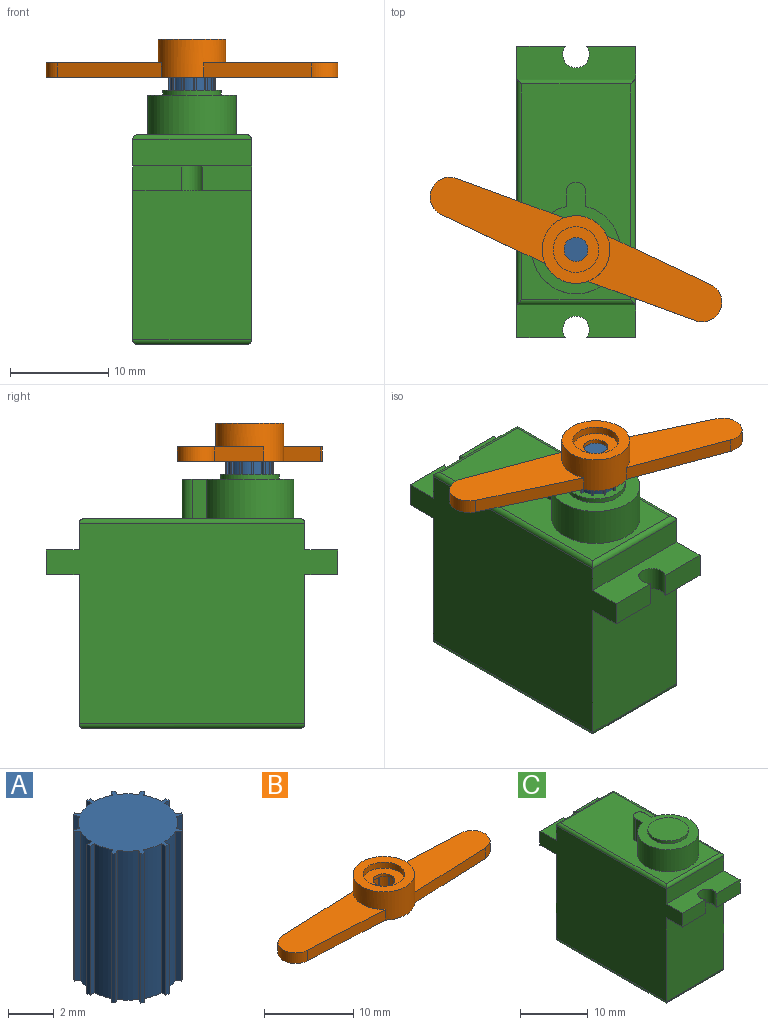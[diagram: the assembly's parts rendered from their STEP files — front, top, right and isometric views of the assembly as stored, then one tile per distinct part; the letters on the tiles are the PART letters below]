
ASSEMBLY  parts=3 mates=2
PART A: 50 faces, bbox 4.9x4.9x8 mm
  f0: cylinder r=2.45mm len=8mm, axis (0,0,-1), area 1.6mm2, adj f1,f2,f3,f4
  f1: plane 8x0.28mm, normal (-1,0,0), area 2.2mm2, adj f0,f3,f4,f5
  f2: plane 8x0.28mm, normal (1,0,0), area 2.2mm2, adj f0,f3,f4,f49
  f3: plane 4.9x4.9mm, normal (0,0,1), area 15.5mm2, adj f0,f1,f2,f5,f6,f7,f8,f9
  f4: plane 4.9x4.9mm, normal (0,0,-1), area 15.5mm2, adj f0,f1,f2,f5,f6,f7,f8,f9
  f5: cylinder r=2.17mm len=8mm, axis (0,0,-1), area 7.5mm2, adj f1,f3,f4,f8
  f6: cylinder r=2.45mm len=8mm, axis (0,0,-1), area 1.6mm2, adj f3,f4,f7,f8
  f7: plane 8x0.24mm, normal (-0.87,-0.5,0), area 2.2mm2, adj f3,f4,f6,f9
  f8: plane 8x0.24mm, normal (0.87,0.5,0), area 2.2mm2, adj f3,f4,f5,f6
  f9: cylinder r=2.17mm len=8mm, axis (0,0,-1), area 7.5mm2, adj f3,f4,f7,f12
  f10: cylinder r=2.45mm len=8mm, axis (0,0,-1), area 1.6mm2, adj f3,f4,f11,f12
  f11: plane 8x0.24mm, normal (-0.5,-0.87,0), area 2.2mm2, adj f3,f4,f10,f13
  f12: plane 8x0.24mm, normal (0.5,0.87,0), area 2.2mm2, adj f3,f4,f9,f10
  f13: cylinder r=2.17mm len=8mm, axis (0,0,-1), area 7.5mm2, adj f3,f4,f11,f16
  f14: cylinder r=2.45mm len=8mm, axis (0,0,-1), area 1.6mm2, adj f3,f4,f15,f16
  f15: plane 8x0.28mm, normal (0,-1,0), area 2.2mm2, adj f3,f4,f14,f17
  f16: plane 8x0.28mm, normal (0,1,0), area 2.2mm2, adj f3,f4,f13,f14
  f17: cylinder r=2.17mm len=8mm, axis (0,0,-1), area 7.5mm2, adj f3,f4,f15,f20
  f18: cylinder r=2.45mm len=8mm, axis (0,0,-1), area 1.6mm2, adj f3,f4,f19,f20
  f19: plane 8x0.24mm, normal (0.5,-0.87,0), area 2.2mm2, adj f3,f4,f18,f21
  f20: plane 8x0.24mm, normal (-0.5,0.87,0), area 2.2mm2, adj f3,f4,f17,f18
  f21: cylinder r=2.17mm len=8mm, axis (0,0,-1), area 7.5mm2, adj f3,f4,f19,f24
  f22: cylinder r=2.45mm len=8mm, axis (0,0,-1), area 1.6mm2, adj f3,f4,f23,f24
  f23: plane 8x0.24mm, normal (0.87,-0.5,0), area 2.2mm2, adj f3,f4,f22,f25
  f24: plane 8x0.24mm, normal (-0.87,0.5,0), area 2.2mm2, adj f3,f4,f21,f22
  f25: cylinder r=2.17mm len=8mm, axis (0,0,-1), area 7.5mm2, adj f3,f4,f23,f28
  f26: cylinder r=2.45mm len=8mm, axis (0,0,-1), area 1.6mm2, adj f3,f4,f27,f28
  f27: plane 8x0.28mm, normal (1,0,0), area 2.2mm2, adj f3,f4,f26,f29
  f28: plane 8x0.28mm, normal (-1,0,0), area 2.2mm2, adj f3,f4,f25,f26
  f29: cylinder r=2.17mm len=8mm, axis (0,0,-1), area 7.5mm2, adj f3,f4,f27,f32
  f30: cylinder r=2.45mm len=8mm, axis (0,0,-1), area 1.6mm2, adj f3,f4,f31,f32
  f31: plane 8x0.24mm, normal (0.87,0.5,0), area 2.2mm2, adj f3,f4,f30,f33
  f32: plane 8x0.24mm, normal (-0.87,-0.5,0), area 2.2mm2, adj f3,f4,f29,f30
  f33: cylinder r=2.17mm len=8mm, axis (0,0,-1), area 7.5mm2, adj f3,f4,f31,f36
  f34: cylinder r=2.45mm len=8mm, axis (0,0,-1), area 1.6mm2, adj f3,f4,f35,f36
  f35: plane 8x0.24mm, normal (0.5,0.87,0), area 2.2mm2, adj f3,f4,f34,f37
  f36: plane 8x0.24mm, normal (-0.5,-0.87,0), area 2.2mm2, adj f3,f4,f33,f34
  f37: cylinder r=2.17mm len=8mm, axis (0,0,-1), area 7.5mm2, adj f3,f4,f35,f40
  f38: cylinder r=2.45mm len=8mm, axis (0,0,-1), area 1.6mm2, adj f3,f4,f39,f40
  f39: plane 8x0.28mm, normal (0,1,0), area 2.2mm2, adj f3,f4,f38,f41
  f40: plane 8x0.28mm, normal (0,-1,0), area 2.2mm2, adj f3,f4,f37,f38
  f41: cylinder r=2.17mm len=8mm, axis (0,0,-1), area 7.5mm2, adj f3,f4,f39,f44
  f42: cylinder r=2.45mm len=8mm, axis (0,0,-1), area 1.6mm2, adj f3,f4,f43,f44
  f43: plane 8x0.24mm, normal (-0.5,0.87,0), area 2.2mm2, adj f3,f4,f42,f45
  f44: plane 8x0.24mm, normal (0.5,-0.87,0), area 2.2mm2, adj f3,f4,f41,f42
  f45: cylinder r=2.17mm len=8mm, axis (0,0,-1), area 7.5mm2, adj f3,f4,f43,f48
  f46: cylinder r=2.45mm len=8mm, axis (0,0,-1), area 1.6mm2, adj f3,f4,f47,f48
  f47: plane 8x0.24mm, normal (-0.87,0.5,0), area 2.2mm2, adj f3,f4,f46,f49
  f48: plane 8x0.24mm, normal (0.87,-0.5,0), area 2.2mm2, adj f3,f4,f45,f46
  f49: cylinder r=2.17mm len=8mm, axis (0,0,-1), area 7.5mm2, adj f2,f3,f4,f47
PART B: 63 faces, bbox 31.9x6.9x3.9 mm
  f0: cylinder r=2.45mm len=2.65mm, axis (0,0,-1), area 0.5mm2, adj f1,f47,f57,f59
  f1: plane 2.65x0.28mm, normal (-1,0,0), area 0.7mm2, adj f0,f2,f57,f59
  f2: cylinder r=2.17mm len=2.65mm, axis (0,0,-1), area 2.5mm2, adj f1,f3,f57,f59
  f3: plane 2.65x0.24mm, normal (0.87,-0.5,0), area 0.7mm2, adj f2,f4,f57,f59
  f4: cylinder r=2.45mm len=2.65mm, axis (0,0,-1), area 0.5mm2, adj f3,f5,f57,f59
  f5: plane 2.65x0.24mm, normal (-0.87,0.5,0), area 0.7mm2, adj f4,f6,f57,f59
  f6: cylinder r=2.17mm len=2.65mm, axis (0,0,-1), area 2.5mm2, adj f5,f7,f57,f59
  f7: plane 2.65x0.24mm, normal (0.5,-0.87,0), area 0.7mm2, adj f6,f8,f57,f59
  f8: cylinder r=2.45mm len=2.65mm, axis (0,0,-1), area 0.5mm2, adj f7,f9,f57,f59
  f9: plane 2.65x0.24mm, normal (-0.5,0.87,0), area 0.7mm2, adj f8,f10,f57,f59
  f10: cylinder r=2.17mm len=2.65mm, axis (0,0,-1), area 2.5mm2, adj f9,f11,f57,f59
  f11: plane 2.65x0.28mm, normal (0,-1,0), area 0.7mm2, adj f10,f12,f57,f59
  f12: cylinder r=2.45mm len=2.65mm, axis (0,0,-1), area 0.5mm2, adj f11,f13,f57,f59
  f13: plane 2.65x0.28mm, normal (0,1,0), area 0.7mm2, adj f12,f14,f57,f59
  f14: cylinder r=2.17mm len=2.65mm, axis (0,0,-1), area 2.5mm2, adj f13,f15,f57,f59
  f15: plane 2.65x0.24mm, normal (-0.5,-0.87,0), area 0.7mm2, adj f14,f16,f57,f59
  f16: cylinder r=2.45mm len=2.65mm, axis (0,0,-1), area 0.5mm2, adj f15,f17,f57,f59
  f17: plane 2.65x0.24mm, normal (0.5,0.87,0), area 0.7mm2, adj f16,f18,f57,f59
  f18: cylinder r=2.17mm len=2.65mm, axis (0,0,-1), area 2.5mm2, adj f17,f19,f57,f59
  f19: plane 2.65x0.24mm, normal (-0.87,-0.5,0), area 0.7mm2, adj f18,f20,f57,f59
  f20: cylinder r=2.45mm len=2.65mm, axis (0,0,-1), area 0.5mm2, adj f19,f21,f57,f59
  f21: plane 2.65x0.24mm, normal (0.87,0.5,0), area 0.7mm2, adj f20,f22,f57,f59
  f22: cylinder r=2.17mm len=2.65mm, axis (0,0,-1), area 2.5mm2, adj f21,f23,f57,f59
  f23: plane 2.65x0.28mm, normal (-1,0,0), area 0.7mm2, adj f22,f24,f57,f59
  f24: cylinder r=2.45mm len=2.65mm, axis (0,0,-1), area 0.5mm2, adj f23,f25,f57,f59
  f25: plane 2.65x0.28mm, normal (1,0,0), area 0.7mm2, adj f24,f26,f57,f59
  f26: cylinder r=2.17mm len=2.65mm, axis (0,0,-1), area 2.5mm2, adj f25,f27,f57,f59
  f27: plane 2.65x0.24mm, normal (-0.87,0.5,0), area 0.7mm2, adj f26,f28,f57,f59
  f28: cylinder r=2.45mm len=2.65mm, axis (0,0,-1), area 0.5mm2, adj f27,f29,f57,f59
  f29: plane 2.65x0.24mm, normal (0.87,-0.5,0), area 0.7mm2, adj f28,f30,f57,f59
  f30: cylinder r=2.17mm len=2.65mm, axis (0,0,-1), area 2.5mm2, adj f29,f31,f57,f59
  f31: plane 2.65x0.24mm, normal (-0.5,0.87,0), area 0.7mm2, adj f30,f32,f57,f59
  f32: cylinder r=2.45mm len=2.65mm, axis (0,0,-1), area 0.5mm2, adj f31,f33,f57,f59
  f33: plane 2.65x0.24mm, normal (0.5,-0.87,0), area 0.7mm2, adj f32,f34,f57,f59
  f34: cylinder r=2.17mm len=2.65mm, axis (0,0,-1), area 2.5mm2, adj f33,f35,f57,f59
  f35: plane 2.65x0.28mm, normal (0,1,0), area 0.7mm2, adj f34,f36,f57,f59
  f36: cylinder r=2.45mm len=2.65mm, axis (0,0,-1), area 0.5mm2, adj f35,f37,f57,f59
  f37: plane 2.65x0.28mm, normal (0,-1,0), area 0.7mm2, adj f36,f38,f57,f59
  f38: cylinder r=2.17mm len=2.65mm, axis (0,0,-1), area 2.5mm2, adj f37,f39,f57,f59
  f39: plane 2.65x0.24mm, normal (0.5,0.87,0), area 0.7mm2, adj f38,f40,f57,f59
  f40: cylinder r=2.45mm len=2.65mm, axis (0,0,-1), area 0.5mm2, adj f39,f41,f57,f59
  f41: plane 2.65x0.24mm, normal (-0.5,-0.87,0), area 0.7mm2, adj f40,f42,f57,f59
  f42: cylinder r=2.17mm len=2.65mm, axis (0,0,-1), area 2.5mm2, adj f41,f43,f57,f59
  f43: plane 2.65x0.24mm, normal (0.87,0.5,0), area 0.7mm2, adj f42,f44,f57,f59
  f44: cylinder r=2.45mm len=2.65mm, axis (0,0,-1), area 0.5mm2, adj f43,f45,f57,f59
  f45: plane 2.65x0.24mm, normal (-0.87,-0.5,0), area 0.7mm2, adj f44,f46,f57,f59
  f46: cylinder r=2.17mm len=2.65mm, axis (0,0,-1), area 2.5mm2, adj f45,f47,f57,f59
  f47: plane 2.65x0.28mm, normal (1,0,0), area 0.7mm2, adj f0,f46,f57,f59
  f48: plane 13.59x5.04mm, normal (0,0,1), area 54.9mm2, adj f49,f50,f51,f55
  f49: cylinder r=2mm len=4mm, axis (0,0,-1), area 8.9mm2, adj f48,f50,f55,f57
  f50: plane 11.68x1.45mm, normal (-0.04,-1,0), area 17mm2, adj f48,f49,f51,f57
  f51: cylinder r=3.45mm len=6.9mm, axis (0,0,-1), area 67.1mm2, adj f48,f50,f52,f54,f55,f56,f57,f58
  f52: plane 11.68x1.45mm, normal (0.04,-1,0), area 17mm2, adj f51,f53,f56,f57
  f53: cylinder r=2mm len=4mm, axis (0,0,-1), area 8.9mm2, adj f52,f54,f56,f57
  f54: plane 11.68x1.45mm, normal (0.04,1,0), area 17mm2, adj f51,f53,f56,f57
  f55: plane 11.68x1.45mm, normal (-0.04,1,0), area 17mm2, adj f48,f49,f51,f57
  f56: plane 13.59x5.04mm, normal (0,0,1), area 54.9mm2, adj f51,f52,f53,f54
  f57: plane 31.9x6.9mm, normal (0,0,-1), area 131.7mm2, adj f0,f1,f2,f3,f4,f5,f6,f7
  f58: plane 6.9x6.9mm, normal (0,0,1), area 20.3mm2, adj f51,f60
  f59: plane 4.9x4.9mm, normal (0,0,-1), area 10.8mm2, adj f0,f1,f2,f3,f4,f5,f6,f7
  f60: cylinder r=2.33mm len=4.66mm, axis (0,0,1), area 11.7mm2, adj f58,f61
  f61: plane 4.66x4.66mm, normal (0,0,1), area 12.4mm2, adj f60,f62
  f62: cylinder r=1.22mm len=2.44mm, axis (0,0,1), area 3.1mm2, adj f59,f61
PART C: 33 faces, bbox 12.1x29.7x25.9 mm
  f0: plane 12.1x2.7mm, normal (0,1,0), area 32.7mm2, adj f4,f6,f16,f29
  f1: plane 12.1x2.7mm, normal (0,-1,0), area 32.7mm2, adj f4,f6,f17,f24
  f2: plane 22x11.1mm, normal (0,0,1), area 176.2mm2, adj f8,f9,f10,f11,f15,f16,f17,f18
  f3: plane 15.2x12.1mm, normal (0,1,0), area 183.9mm2, adj f4,f6,f20,f30
  f4: plane 29.69x20.4mm, normal (-1,0,0), area 485.9mm2, adj f0,f1,f3,f5,f15,f19,f24,f25
  f5: plane 15.2x12.1mm, normal (0,-1,0), area 183.9mm2, adj f4,f6,f21,f25
  f6: plane 29.69x20.4mm, normal (1,0,0), area 485.9mm2, adj f0,f1,f3,f5,f18,f22,f23,f24
  f7: plane 22x11.1mm, normal (0,0,-1), area 244.2mm2, adj f19,f20,f21,f22
  f8: plane 4x1.5mm, normal (1,0,0), area 6mm2, adj f2,f9,f11,f12
  f9: cylinder r=1mm len=4mm, axis (0,0,-1), area 12.6mm2, adj f2,f8,f10,f12
  f10: plane 4x1.5mm, normal (-1,0,0), area 6mm2, adj f2,f9,f11,f12
  f11: cylinder r=4.5mm len=9mm, axis (0,0,-1), area 105mm2, adj f2,f8,f10,f12
  f12: plane 11.39x9mm, normal (0,0,1), area 39.9mm2, adj f8,f9,f10,f11,f13
  f13: cylinder r=2.99mm len=5.98mm, axis (0,0,-1), area 9.4mm2, adj f12,f14
  f14: plane 5.98x5.98mm, normal (0,0,1), area 28.1mm2, adj f13
  f15: cylinder r=0.5mm len=23mm, axis (0,1,0), area 17.8mm2, adj f2,f4,f16,f17
  f16: cylinder r=0.5mm len=12.1mm, axis (1,0,0), area 9.2mm2, adj f0,f2,f15,f18
  f17: cylinder r=0.5mm len=12.1mm, axis (-1,0,0), area 9.2mm2, adj f1,f2,f15,f18
  f18: cylinder r=0.5mm len=23mm, axis (0,-1,0), area 17.8mm2, adj f2,f6,f16,f17
  f19: cylinder r=0.5mm len=23mm, axis (0,-1,0), area 17.8mm2, adj f4,f7,f20,f21
  f20: cylinder r=0.5mm len=12.1mm, axis (-1,0,0), area 9.2mm2, adj f3,f7,f19,f22
  f21: cylinder r=0.5mm len=12.1mm, axis (1,0,0), area 9.2mm2, adj f5,f7,f19,f22
  f22: cylinder r=0.5mm len=23mm, axis (0,1,0), area 17.8mm2, adj f6,f7,f20,f21
  f23: plane 5.01x2.5mm, normal (0,-1,0), area 12.5mm2, adj f6,f24,f25,f27
  f24: plane 12.1x3.35mm, normal (0,0,1), area 35.5mm2, adj f1,f4,f6,f23,f26,f27
  f25: plane 12.1x3.35mm, normal (0,0,-1), area 35.5mm2, adj f4,f5,f6,f23,f26,f27
  f26: plane 4.98x2.5mm, normal (0,-1,0), area 12.5mm2, adj f4,f24,f25,f27
  f27: cylinder r=1.35mm len=2.7mm, axis (0,0,-1), area 15.2mm2, adj f23,f24,f25,f26
  f28: plane 5.01x2.5mm, normal (0,1,0), area 12.5mm2, adj f6,f29,f30,f32
  f29: plane 12.1x3.35mm, normal (0,0,1), area 35.5mm2, adj f0,f4,f6,f28,f31,f32
  f30: plane 12.1x3.35mm, normal (0,0,-1), area 35.5mm2, adj f3,f4,f6,f28,f31,f32
  f31: plane 4.98x2.5mm, normal (0,1,0), area 12.5mm2, adj f4,f29,f30,f32
  f32: cylinder r=1.35mm len=2.7mm, axis (0,0,-1), area 15.2mm2, adj f28,f29,f30,f31
PLACE A rot(axis=(0,0,-1),22.6deg) t=(-0.77,0.98,0.56)mm
PLACE B rot(axis=(0,0,-1),22.6deg) t=(-0.77,0.98,-2.09)mm
PLACE C t=(-3.03,1.43,0.06)mm fixed
MATE revolute A.f0 <-> C.f11  axis (0,0,-1) through (-3.03,-4.46,15.26)mm
MATE fastened A.f0 <-> B.f0  axis (0,0,1) through (-3.03,-4.46,19.26)mm
